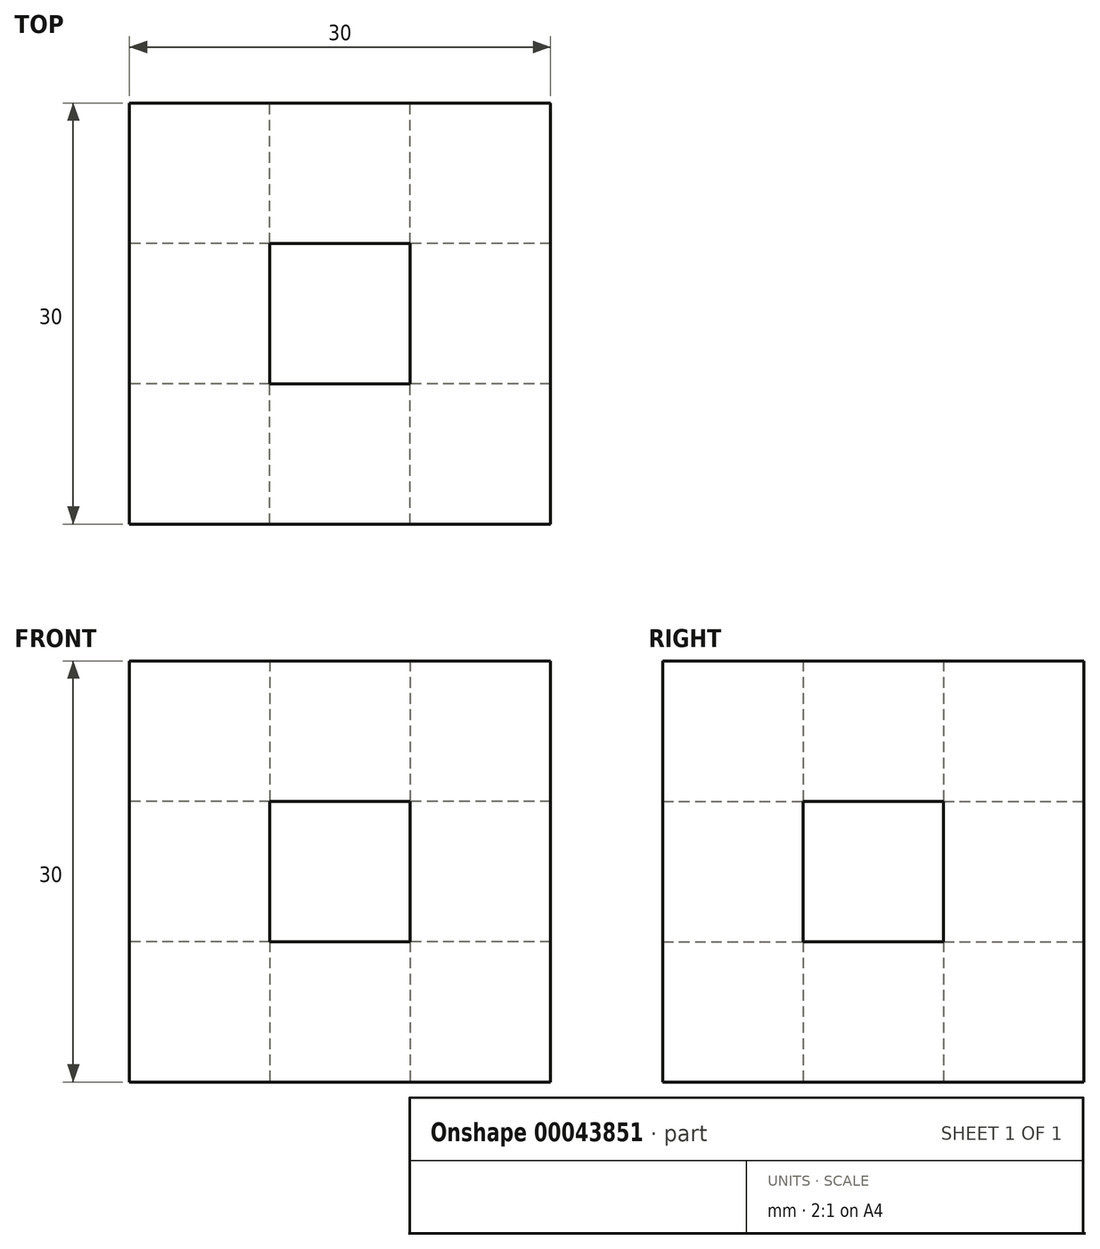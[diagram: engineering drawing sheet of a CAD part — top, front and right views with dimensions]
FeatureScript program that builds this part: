
annotation { "Feature Type Name" : "Feature", "Feature Type Description" : "" }
export const myFeature = defineFeature(function(context is Context, id is Id, definition is map)
    precondition{}
    {
        {
            assignVariable(context, id + "F0", {"name" : "width", "anyValue" : 30});
        }
        {
            var Q0;
            Q0=qCreatedBy(makeId("Top.planeOp"),FACE);
            var sketch = newSketch(context, id + "F1", { "sketchPlane" : qUnion([Q0])});
            skLineSegment(sketch, "E0.bottom", {"start": v(15, -15) * mm, "end": v(-15, -15) * mm});
            skLineSegment(sketch, "E0.top", {"start": v(15, 15) * mm, "end": v(-15, 15) * mm});
            skLineSegment(sketch, "E0.left", {"start": v(15, -15) * mm, "end": v(15, 15) * mm});
            skLineSegment(sketch, "E0.right", {"start": v(-15, -15) * mm, "end": v(-15, 15) * mm});
            skPoint(sketch, "E0.middle", {"position": v(0, 0) * mm});
            skLineSegment(sketch, "E1.bottom", {"start": v(5, -5) * mm, "end": v(-5, -5) * mm});
            skLineSegment(sketch, "E1.top", {"start": v(5, 5) * mm, "end": v(-5, 5) * mm});
            skLineSegment(sketch, "E1.left", {"start": v(5, -5) * mm, "end": v(5, 5) * mm});
            skLineSegment(sketch, "E1.right", {"start": v(-5, -5) * mm, "end": v(-5, 5) * mm});
            skLineSegment(sketch, "E2", {"start": v(-5, 0) * mm, "end": v(-15, 0) * mm, "construction": true});
            skLineSegment(sketch, "E3", {"start": v(-5, 0) * mm, "end": v(5, 0) * mm, "construction": true});
            skSolve(sketch);
        }
        {
            var Q0;
            Q0=makeQuery(id+"F1.imprint","IMPRINT",FACE,{"disambiguationData":[TD([[makeQuery(id+"F1.imprint","IMPRINT",EDGE,{"derivedFrom":sQuery(id+"F1.wireOp",EDGE,"E0.bottom")}),-1.0]])]});
            extrude(context, id + "F2", {"entities" : qUnion([Q0]), "depth" : getVariable(context, 'width') * mm});
        }
        {
            var Q0;
            Q0=makeQuery(id+"F2.opExtrude","SWEPT_FACE",FACE,{"disambiguationData":[OSD([sQuery(id+"F1.wireOp",EDGE,"E0.top")])]});
            var sketch = newSketch(context, id + "F3", { "sketchPlane" : qUnion([Q0])});
            skLineSegment(sketch, "E4.0", {"start": v(-5, 30) * mm, "end": v(-5, 0) * mm});
            skLineSegment(sketch, "E5.0", {"start": v(5, 30) * mm, "end": v(5, 0) * mm});
            skLineSegment(sketch, "E6", {"start": v(-15, 30) * mm, "end": v(15, 0) * mm, "construction": true});
            skLineSegment(sketch, "E7", {"start": v(-5, 20) * mm, "end": v(5, 20) * mm});
            skLineSegment(sketch, "E8", {"start": v(5, 20) * mm, "end": v(5, 10) * mm});
            skLineSegment(sketch, "E9", {"start": v(5, 10) * mm, "end": v(-5, 10) * mm});
            skSolve(sketch);
        }
        {
            var Q0;
            {var subQ0=sQuery(id+"F3.wireOp",EDGE,"E7");Q0=makeQuery(id+"F3.imprint","IMPRINT",FACE,{"disambiguationData":[TD([[makeQuery(id+"F3.imprint","IMPRINT",EDGE,{"derivedFrom":subQ0}),-1.0]])]});}
            var Q1;
            Q1=makeQuery(id+"F2.opExtrude","SWEPT_FACE",FACE,{"disambiguationData":[OSD([sQuery(id+"F1.wireOp",EDGE,"E0.bottom")])]});
            extrude(context, id + "F4", {"entities" : qUnion([Q0]), "operationType" : NewBodyOperationType.REMOVE, "endBound" : BoundingType.UP_TO_SURFACE, "oppositeDirection" : true, "endBoundEntityFace" : qUnion([Q1]), "depth" : 25 * mm});
        }
        {
            var Q0;
            Q0=makeQuery(id+"F2.opExtrude","SWEPT_FACE",FACE,{"disambiguationData":[OSD([sQuery(id+"F1.wireOp",EDGE,"E0.right")])]});
            var sketch = newSketch(context, id + "F5", { "sketchPlane" : qUnion([Q0])});
            skLineSegment(sketch, "E10.0", {"start": v(-15, 30) * mm, "end": v(-15, 0) * mm});
            skLineSegment(sketch, "E11.0.0", {"start": v(-5, 30) * mm, "end": v(-5, 20) * mm, "construction": true});
            skLineSegment(sketch, "E11.0.1", {"start": v(-5, 20) * mm, "end": v(-15, 20) * mm, "construction": true});
            skLineSegment(sketch, "E11.0.2", {"start": v(-15, 20) * mm, "end": v(-15, 10) * mm, "construction": true});
            skLineSegment(sketch, "E11.0.3", {"start": v(-15, 10) * mm, "end": v(-5, 10) * mm, "construction": true});
            skLineSegment(sketch, "E11.0.4", {"start": v(-5, 10) * mm, "end": v(-5, 0) * mm, "construction": true});
            skLineSegment(sketch, "E11.0.5", {"start": v(-5, 0) * mm, "end": v(5, 0) * mm, "construction": true});
            skLineSegment(sketch, "E11.0.6", {"start": v(5, 0) * mm, "end": v(5, 10) * mm, "construction": true});
            skLineSegment(sketch, "E11.0.7", {"start": v(5, 10) * mm, "end": v(15, 10) * mm, "construction": true});
            skLineSegment(sketch, "E11.0.8", {"start": v(15, 10) * mm, "end": v(15, 20) * mm, "construction": true});
            skLineSegment(sketch, "E11.0.9", {"start": v(15, 20) * mm, "end": v(5, 20) * mm, "construction": true});
            skLineSegment(sketch, "E11.0.10", {"start": v(5, 20) * mm, "end": v(5, 30) * mm, "construction": true});
            skLineSegment(sketch, "E11.0.11", {"start": v(5, 30) * mm, "end": v(-5, 30) * mm, "construction": true});
            skLineSegment(sketch, "E12", {"start": v(5, 20) * mm, "end": v(-5, 20) * mm});
            skLineSegment(sketch, "E13", {"start": v(-5, 10) * mm, "end": v(-5, 20) * mm});
            skLineSegment(sketch, "E14", {"start": v(-5, 10) * mm, "end": v(5, 10) * mm});
            skLineSegment(sketch, "E15", {"start": v(5, 20) * mm, "end": v(5, 10) * mm});
            skSolve(sketch);
        }
        {
            var Q0;
            Q0=makeQuery(id+"F5.imprint","IMPRINT",FACE,{"disambiguationData":[TD([[makeQuery(id+"F5.imprint","IMPRINT",EDGE,{"derivedFrom":sQuery(id+"F5.wireOp",EDGE,"E12")}),1.0]])]});
            var Q1;
            Q1=makeQuery(id+"F2.opExtrude","SWEPT_FACE",FACE,{"disambiguationData":[OSD([sQuery(id+"F1.wireOp",EDGE,"E0.left")])]});
            extrude(context, id + "F6", {"entities" : qUnion([Q0]), "operationType" : NewBodyOperationType.REMOVE, "endBound" : BoundingType.UP_TO_SURFACE, "oppositeDirection" : true, "endBoundEntityFace" : qUnion([Q1]), "depth" : 25 * mm});
        }
    });
